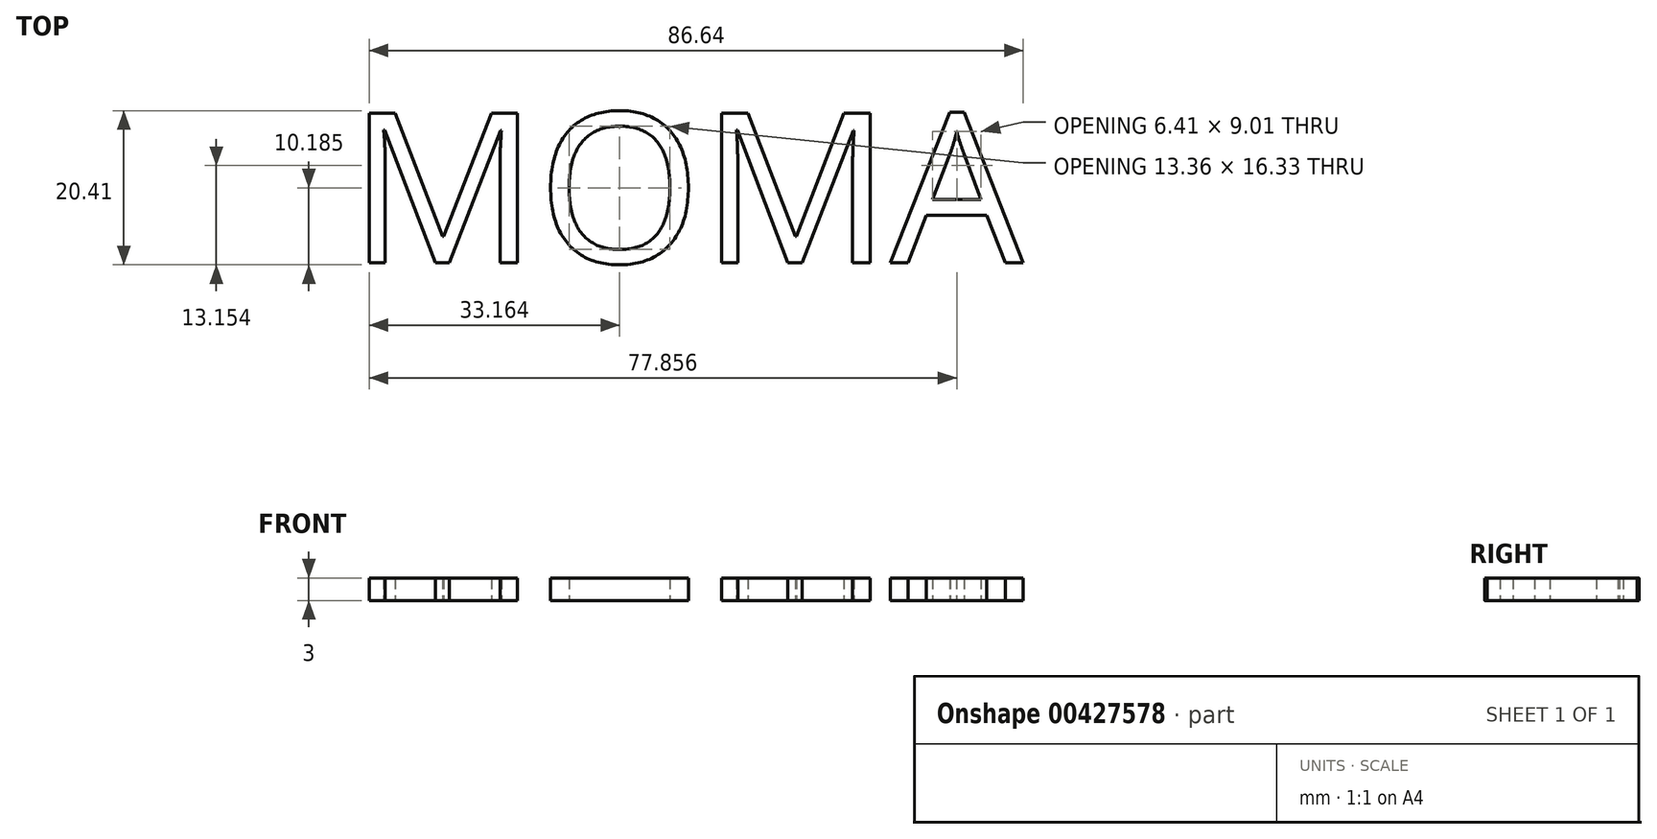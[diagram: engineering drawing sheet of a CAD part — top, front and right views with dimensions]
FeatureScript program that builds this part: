
annotation { "Feature Type Name" : "Feature", "Feature Type Description" : "" }
export const myFeature = defineFeature(function(context is Context, id is Id, definition is map)
    precondition{}
    {
        {
            var Q0;
            Q0=qCreatedBy(makeId("Top.planeOp"),FACE);
            var sketch = newSketch(context, id + "F0", { "sketchPlane" : qUnion([Q0])});
            skText(sketch, "E0", { "text": "MOMA", "fontName": "OpenSans-Regular.ttf"});
            const initialGuessF0  = {"E0": [0, 0, 1, 0, 0.02]};
            skSetInitialGuess(sketch, initialGuessF0);
            skSolve(sketch);
        }
        {
            var Q0;
            Q0 = qSketchRegion(id + "F0", true);
            extrude(context, id + "F1", {"entities" : qUnion([Q0]), "depth" : 3 * mm});
        }
    });
